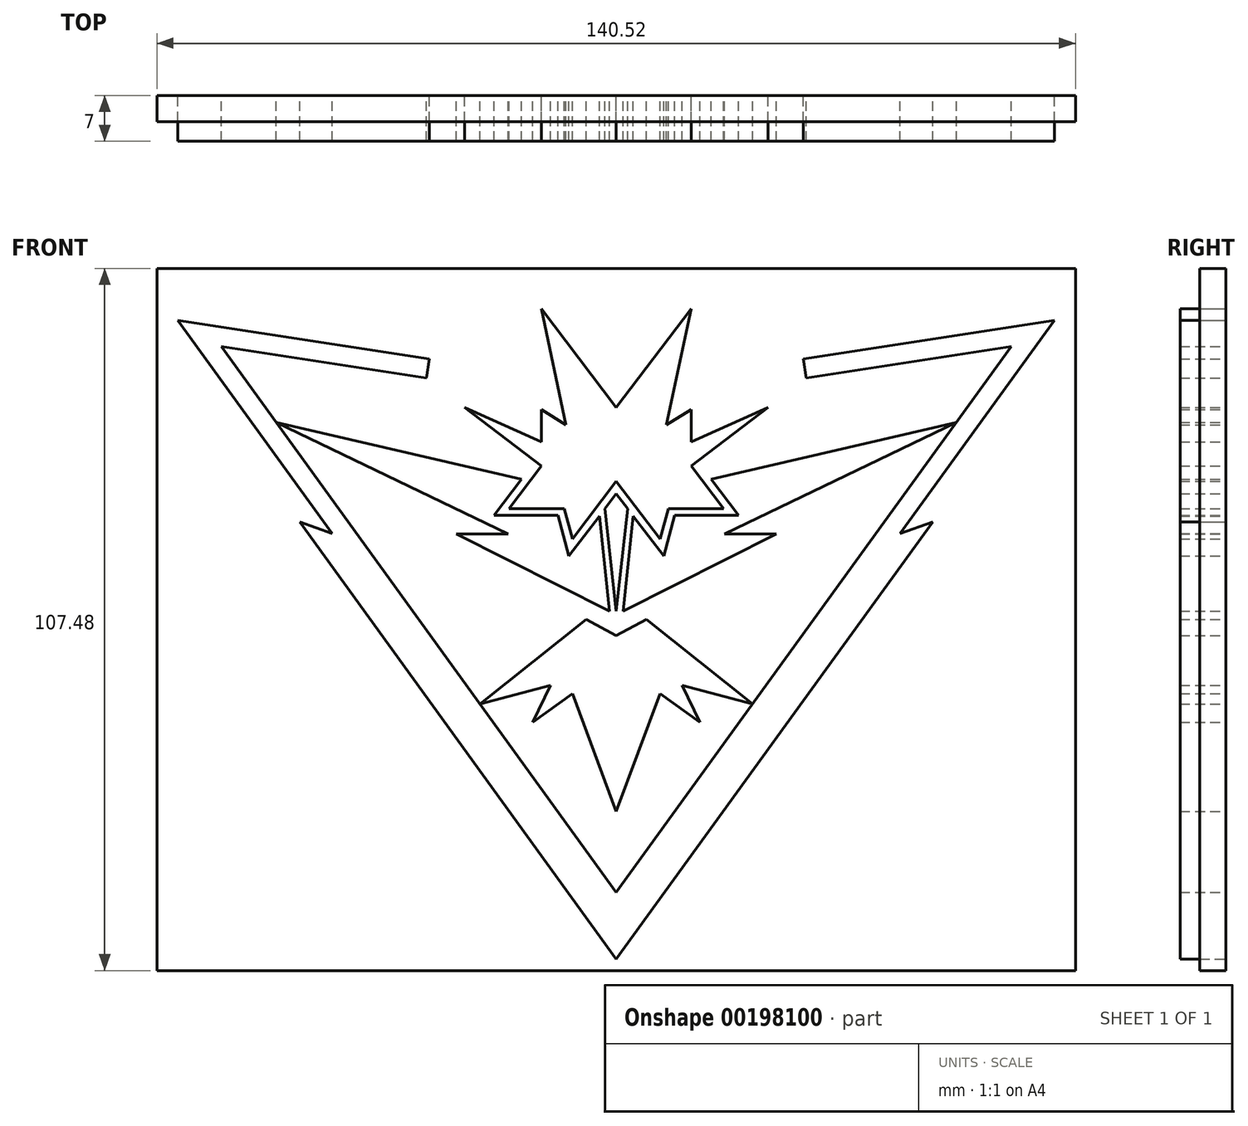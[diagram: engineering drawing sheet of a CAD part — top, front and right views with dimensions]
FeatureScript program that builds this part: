
annotation { "Feature Type Name" : "Feature", "Feature Type Description" : "" }
export const myFeature = defineFeature(function(context is Context, id is Id, definition is map)
    precondition{}
    {
        {
            var Q0;
            Q0=qCreatedBy(makeId("Front.planeOp"),FACE);
            var sketch = newSketch(context, id + "F0", { "sketchPlane" : qUnion([Q0])});
            skLineSegment(sketch, "E0", {"start": v(-60.42, 41.78) * mm, "end": v(0, -41.78) * mm});
            skLineSegment(sketch, "E1", {"start": v(-60.42, 36.66) * mm, "end": v(-43.44, 13.18) * mm});
            skLineSegment(sketch, "E2", {"start": v(-43.44, 13.18) * mm, "end": v(-48.4, 14.93) * mm});
            skLineSegment(sketch, "E3", {"start": v(-48.4, 14.93) * mm, "end": v(0, -52.02) * mm});
            skLineSegment(sketch, "E4", {"start": v(-60.42, 36.66) * mm, "end": v(-66.3, 44.78) * mm});
            skLineSegment(sketch, "E5", {"start": v(0, -2.45) * mm, "end": v(-4.6, 0) * mm});
            skLineSegment(sketch, "E6", {"start": v(-4.6, 0) * mm, "end": v(-20.87, -12.9) * mm});
            skLineSegment(sketch, "E7", {"start": v(-20.87, -12.9) * mm, "end": v(-10.07, -10.07) * mm});
            skLineSegment(sketch, "E8", {"start": v(-10.07, -10.07) * mm, "end": v(-12.8, -15.76) * mm});
            skLineSegment(sketch, "E9", {"start": v(-12.8, -15.76) * mm, "end": v(-6.71, -11.35) * mm});
            skLineSegment(sketch, "E10", {"start": v(-6.71, -11.35) * mm, "end": v(0, -29.36) * mm});
            skLineSegment(sketch, "E11", {"start": v(-24.47, 13.08) * mm, "end": v(-16.56, 13.08) * mm});
            skLineSegment(sketch, "E12", {"start": v(-16.56, 13.08) * mm, "end": v(-52.03, 30.18) * mm});
            skLineSegment(sketch, "E13", {"start": v(-52.03, 30.18) * mm, "end": v(-14.52, 21.5) * mm});
            skLineSegment(sketch, "E14", {"start": v(0, 1.3) * mm, "end": v(-1.76, 16.95) * mm});
            skLineSegment(sketch, "E15", {"start": v(0, 32.47) * mm, "end": v(-11.45, 47.55) * mm});
            skLineSegment(sketch, "E16", {"start": v(-11.45, 47.55) * mm, "end": v(-7.67, 29.83) * mm});
            skLineSegment(sketch, "E17", {"start": v(-7.67, 29.83) * mm, "end": v(-11.45, 32.15) * mm});
            skLineSegment(sketch, "E18", {"start": v(-11.45, 32.15) * mm, "end": v(-11.45, 27.21) * mm});
            skLineSegment(sketch, "E19", {"start": v(-11.45, 27.21) * mm, "end": v(-23.23, 32.47) * mm});
            skLineSegment(sketch, "E20", {"start": v(-23.23, 32.47) * mm, "end": v(-11.45, 23.53) * mm});
            skLineSegment(sketch, "E21", {"start": v(-11.45, 23.53) * mm, "end": v(-16.43, 16.97) * mm});
            skLineSegment(sketch, "E22", {"start": v(-16.43, 16.97) * mm, "end": v(-7.95, 16.97) * mm});
            skLineSegment(sketch, "E23", {"start": v(-2.6, 15.85) * mm, "end": v(-7.25, 9.7) * mm});
            skLineSegment(sketch, "E24", {"start": v(0, 21.14) * mm, "end": v(-6.7, 12.32) * mm});
            skLineSegment(sketch, "E25", {"start": v(-6.7, 12.32) * mm, "end": v(-7.95, 16.97) * mm});
            skLineSegment(sketch, "E26", {"start": v(-1.76, 16.95) * mm, "end": v(0, 19.27) * mm});
            skLineSegment(sketch, "E27", {"start": v(-7.25, 9.7) * mm, "end": v(-8.94, 15.97) * mm});
            skLineSegment(sketch, "E28", {"start": v(-8.94, 15.97) * mm, "end": v(-16.94, 15.97) * mm});
            skLineSegment(sketch, "E29", {"start": v(-16.94, 15.97) * mm, "end": v(-18.72, 15.97) * mm});
            skLineSegment(sketch, "E30", {"start": v(-18.72, 15.97) * mm, "end": v(-14.52, 21.5) * mm});
            skPoint(sketch, "E31.orphan", {"position": v(-13.23, 21.2) * mm});
            skLineSegment(sketch, "E32", {"start": v(-60.42, 41.78) * mm, "end": v(-29.07, 36.96) * mm});
            skLineSegment(sketch, "E33", {"start": v(-29.07, 36.96) * mm, "end": v(-28.61, 39.93) * mm});
            skLineSegment(sketch, "E34", {"start": v(-28.61, 39.93) * mm, "end": v(-62.2, 45.08) * mm});
            skLineSegment(sketch, "E35", {"start": v(-66.3, 44.78) * mm, "end": v(-67.05, 45.83) * mm});
            skLineSegment(sketch, "E36", {"start": v(-67.05, 45.83) * mm, "end": v(-62.2, 45.08) * mm});
            skPoint(sketch, "E37.orphan", {"position": v(-60.42, -41.78) * mm});
            skLineSegment(sketch, "E38", {"start": v(0, 1.3) * mm, "end": v(-0.58, 6.42) * mm});
            skLineSegment(sketch, "E39", {"start": v(-24.47, 13.08) * mm, "end": v(-1.07, 1.3) * mm});
            skLineSegment(sketch, "E40", {"start": v(-1.07, 1.3) * mm, "end": v(-2.6, 15.85) * mm});
            skLineSegment(sketch, "E41.MirrorCS", {"start": v(0, 32.47) * mm, "end": v(11.45, 47.55) * mm});
            skLineSegment(sketch, "E42.MirrorCS", {"start": v(11.45, 47.55) * mm, "end": v(7.67, 29.83) * mm});
            skLineSegment(sketch, "E43.MirrorCS", {"start": v(7.67, 29.83) * mm, "end": v(11.45, 32.15) * mm});
            skLineSegment(sketch, "E44.MirrorCS", {"start": v(11.45, 32.15) * mm, "end": v(11.45, 27.21) * mm});
            skLineSegment(sketch, "E45.MirrorCS", {"start": v(11.45, 27.21) * mm, "end": v(23.23, 32.47) * mm});
            skLineSegment(sketch, "E46.MirrorCS", {"start": v(23.23, 32.47) * mm, "end": v(11.45, 23.53) * mm});
            skLineSegment(sketch, "E47.MirrorCS", {"start": v(11.45, 23.53) * mm, "end": v(16.43, 16.97) * mm});
            skLineSegment(sketch, "E48.MirrorCS", {"start": v(16.43, 16.97) * mm, "end": v(7.95, 16.97) * mm});
            skLineSegment(sketch, "E49.MirrorCS", {"start": v(6.7, 12.32) * mm, "end": v(7.95, 16.97) * mm});
            skLineSegment(sketch, "E50.MirrorCS", {"start": v(0, 21.14) * mm, "end": v(6.7, 12.32) * mm});
            skLineSegment(sketch, "E51.MirrorCS", {"start": v(1.76, 16.95) * mm, "end": v(0, 19.27) * mm});
            skLineSegment(sketch, "E52.MirrorCS", {"start": v(0, 1.3) * mm, "end": v(1.76, 16.95) * mm});
            skLineSegment(sketch, "E53.MirrorCS", {"start": v(0, -2.45) * mm, "end": v(4.6, 0) * mm});
            skLineSegment(sketch, "E54.MirrorCS", {"start": v(4.6, 0) * mm, "end": v(20.87, -12.9) * mm});
            skLineSegment(sketch, "E55.MirrorCS", {"start": v(20.87, -12.9) * mm, "end": v(10.07, -10.07) * mm});
            skLineSegment(sketch, "E56.MirrorCS", {"start": v(10.07, -10.07) * mm, "end": v(12.8, -15.76) * mm});
            skLineSegment(sketch, "E57.MirrorCS", {"start": v(12.8, -15.76) * mm, "end": v(6.71, -11.35) * mm});
            skLineSegment(sketch, "E58.MirrorCS", {"start": v(6.71, -11.35) * mm, "end": v(0, -29.36) * mm});
            skLineSegment(sketch, "E59.MirrorCS", {"start": v(60.42, 41.78) * mm, "end": v(0, -41.78) * mm});
            skLineSegment(sketch, "E60.MirrorCS", {"start": v(48.4, 14.93) * mm, "end": v(0, -52.02) * mm});
            skLineSegment(sketch, "E61.MirrorCS", {"start": v(43.44, 13.18) * mm, "end": v(48.4, 14.93) * mm});
            skLineSegment(sketch, "E62.MirrorCS", {"start": v(60.42, 36.66) * mm, "end": v(43.44, 13.18) * mm});
            skLineSegment(sketch, "E63.MirrorCS", {"start": v(60.42, 36.66) * mm, "end": v(66.3, 44.78) * mm});
            skLineSegment(sketch, "E64.MirrorCS", {"start": v(28.61, 39.93) * mm, "end": v(62.2, 45.08) * mm});
            skLineSegment(sketch, "E65.MirrorCS", {"start": v(60.42, 41.78) * mm, "end": v(29.07, 36.96) * mm});
            skLineSegment(sketch, "E66.MirrorCS", {"start": v(67.05, 45.83) * mm, "end": v(62.2, 45.08) * mm});
            skLineSegment(sketch, "E67.MirrorCS", {"start": v(29.07, 36.96) * mm, "end": v(28.61, 39.93) * mm});
            skLineSegment(sketch, "E68.MirrorCS", {"start": v(52.03, 30.18) * mm, "end": v(14.52, 21.5) * mm});
            skLineSegment(sketch, "E69.MirrorCS", {"start": v(16.56, 13.08) * mm, "end": v(52.03, 30.18) * mm});
            skLineSegment(sketch, "E70.MirrorCS", {"start": v(8.94, 15.97) * mm, "end": v(16.94, 15.97) * mm});
            skLineSegment(sketch, "E71.MirrorCS", {"start": v(7.25, 9.7) * mm, "end": v(8.94, 15.97) * mm});
            skLineSegment(sketch, "E72.MirrorCS", {"start": v(2.6, 15.85) * mm, "end": v(7.25, 9.7) * mm});
            skLineSegment(sketch, "E73.MirrorCS", {"start": v(1.07, 1.3) * mm, "end": v(2.6, 15.85) * mm});
            skLineSegment(sketch, "E74.MirrorCS", {"start": v(24.47, 13.08) * mm, "end": v(1.07, 1.3) * mm});
            skLineSegment(sketch, "E75.MirrorCS", {"start": v(24.47, 13.08) * mm, "end": v(16.56, 13.08) * mm});
            skLineSegment(sketch, "E76.MirrorCS", {"start": v(18.72, 15.97) * mm, "end": v(14.52, 21.5) * mm});
            skLineSegment(sketch, "E77", {"start": v(16.94, 15.97) * mm, "end": v(18.72, 15.97) * mm});
            skLineSegment(sketch, "E78", {"start": v(66.3, 44.78) * mm, "end": v(67.05, 45.83) * mm});
            skSolve(sketch);
        }
        {
            var Q0;
            Q0=makeQuery(id+"F0.imprint","IMPRINT",FACE,{"disambiguationData":[TD([[makeQuery(id+"F0.imprint","IMPRINT",EDGE,{"derivedFrom":sQuery(id+"F0.wireOp",EDGE,"E15")}),1.0]])]});
            var Q1;
            Q1=makeQuery(id+"F0.imprint","IMPRINT",FACE,{"disambiguationData":[TD([[makeQuery(id+"F0.imprint","IMPRINT",EDGE,{"derivedFrom":sQuery(id+"F0.wireOp",EDGE,"E11")}),-1.0]])]});
            var Q2;
            Q2=makeQuery(id+"F0.imprint","IMPRINT",FACE,{"disambiguationData":[TD([[makeQuery(id+"F0.imprint","IMPRINT",EDGE,{"derivedFrom":sQuery(id+"F0.wireOp",EDGE,"E14")}),-1.0]])]});
            var Q3;
            Q3=makeQuery(id+"F0.imprint","IMPRINT",FACE,{"disambiguationData":[TD([[makeQuery(id+"F0.imprint","IMPRINT",EDGE,{"derivedFrom":sQuery(id+"F0.wireOp",EDGE,"E68.MirrorCS")}),1.0]])]});
            var Q4;
            Q4=makeQuery(id+"F0.imprint","IMPRINT",FACE,{"disambiguationData":[TD([[makeQuery(id+"F0.imprint","IMPRINT",EDGE,{"derivedFrom":sQuery(id+"F0.wireOp",EDGE,"E1")}),1.0]])]});
            var Q5;
            Q5=makeQuery(id+"F0.imprint","IMPRINT",FACE,{"disambiguationData":[TD([[makeQuery(id+"F0.imprint","IMPRINT",EDGE,{"derivedFrom":sQuery(id+"F0.wireOp",EDGE,"E5")}),1.0]])]});
            extrude(context, id + "F1", {"entities" : qUnion([Q0, Q1, Q2, Q3, Q4, Q5]), "depth" : 7 * mm});
        }
        {
            var Q0;
            Q0=qCreatedBy(makeId("Front.planeOp"),FACE);
            var sketch = newSketch(context, id + "F2", { "sketchPlane" : qUnion([Q0])});
            skLineSegment(sketch, "E79.bottom", {"start": v(70.26, 53.74) * mm, "end": v(-70.26, 53.74) * mm});
            skLineSegment(sketch, "E79.top", {"start": v(70.26, -53.74) * mm, "end": v(-70.26, -53.74) * mm});
            skLineSegment(sketch, "E79.left", {"start": v(70.26, 53.74) * mm, "end": v(70.26, -53.74) * mm});
            skLineSegment(sketch, "E79.right", {"start": v(-70.26, 53.74) * mm, "end": v(-70.26, -53.74) * mm});
            skPoint(sketch, "E79.middle", {"position": v(0, 0) * mm});
            skSolve(sketch);
        }
        {
            var Q0;
            Q0=makeQuery(id+"F2.imprint","IMPRINT",FACE,{"disambiguationData":[TD([[makeQuery(id+"F2.imprint","IMPRINT",EDGE,{"derivedFrom":sQuery(id+"F2.wireOp",EDGE,"E79.bottom")}),1.0]])]});
            extrude(context, id + "F3", {"entities" : qUnion([Q0]), "depth" : 4 * mm});
        }
    });
